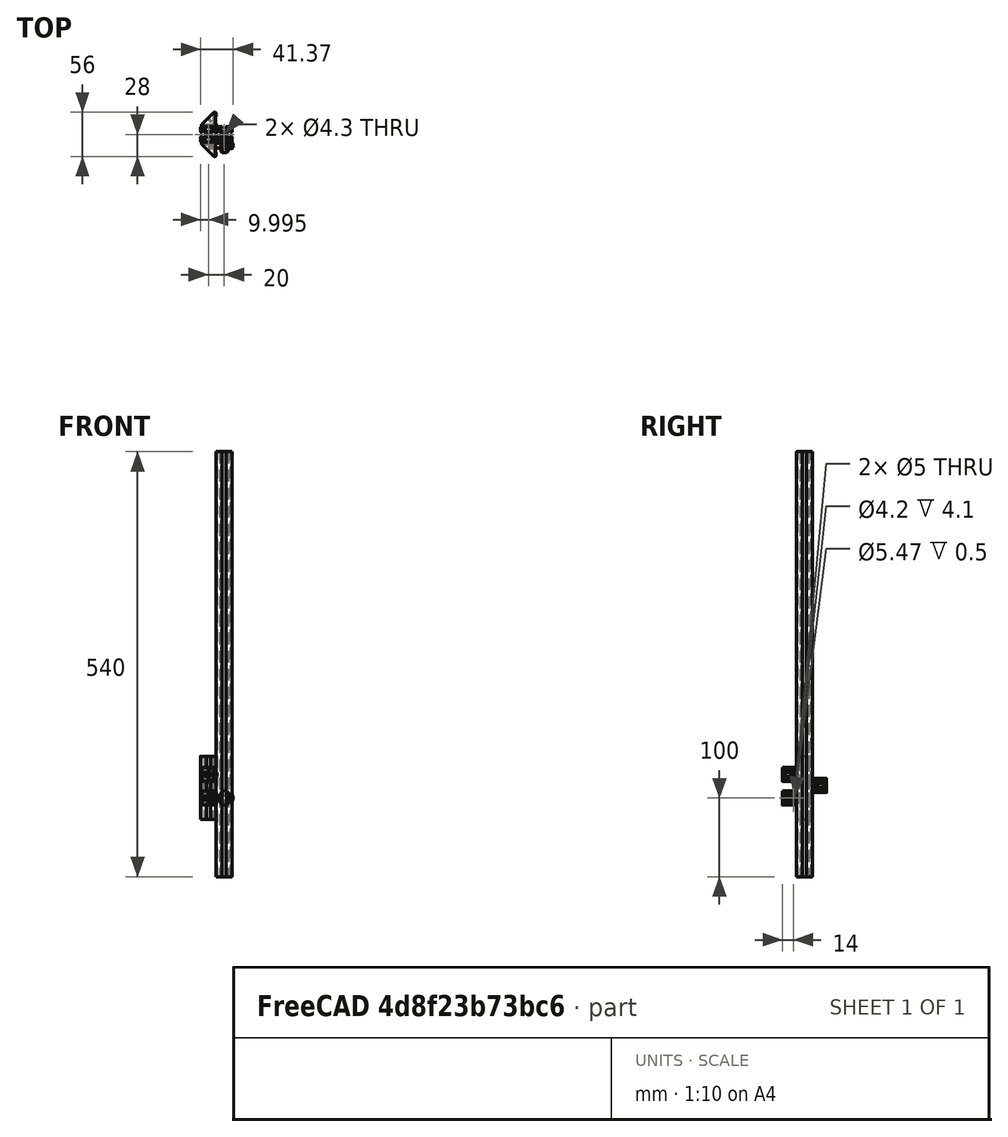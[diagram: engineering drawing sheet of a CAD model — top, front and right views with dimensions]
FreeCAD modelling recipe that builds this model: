
FCSTD DOCUMENT  (FreeCAD 0.19R)
Label: Cart
License: All rights reserved
LicenseURL: http://en.wikipedia.org/wiki/All_rights_reserved
objects: Part::Feature×11, Part::FeaturePython×6, App::Part×4, Part::Cylinder×3
note: 20 computed .brp shape members not serialized (recipe doc carries the construction recipe); baked Part::Feature solids carry a one-line shape summary decoded from their .brp

FEATURE [Part::FeaturePython] Screw001  label="M5x25-Screw"  # Fasteners workbench fastener (typed FeaturePython)
  Placement = pos=(-13,0,0) rot=(0,-1,0;1.5708rad)
  diameter = 3
  invert = false
  length = 5
  lengthCustom = 25
  matchOuter = false
  offset = 1
  thread = false
  type = 12
FEATURE [Part::Cylinder] Cylinder004  label="Spacer"
  Angle = 360
  AttacherType = Attacher::AttachEngine3D
  Height = 6
  Placement = pos=(-10,0,0) rot=(0,1,0;1.5708rad)
  Radius = 3.5
FEATURE [Part::Feature] Cut002  label="Tire"
  Placement = pos=(1,0,0) rot=(0,0,1;0rad)
  shape: bbox 8.8 x 18.03 x 18.03 mm, 6 faces (baked)
FEATURE [Part::Feature] Cut001001  label="Bearing"
  Placement = pos=(1,0,0) rot=(0,0,1;0rad)
  shape: bbox 10 x 10 x 10 mm, 4 faces (baked)
FEATURE [Part::FeaturePython] Nut  label="M5-Nut"  # Fasteners workbench fastener (typed FeaturePython)
  Placement = pos=(11,0,0) rot=(0,-1,0;1.5708rad)
  diameter = 3
  invert = false
  matchOuter = false
  offset = 0
  thread = false
  type = 5
FEATURE [App::Part] Part  label="Rollensatz_Aliexpress4000394459605"
  Group = -> [Screw001,Cut002,Cut001001,Cylinder004,Nut]
  Origin = -> Origin
  Placement = pos=(0,-4,0) rot=(0,0,1;0rad)
FEATURE [Part::FeaturePython] Nut001  label="M5-Nut001"  # Fasteners workbench fastener (typed FeaturePython)
  Placement = pos=(11,0,0) rot=(0,-1,0;1.5708rad)
  diameter = 3
  invert = false
  matchOuter = false
  offset = 0
  thread = false
  type = 5
FEATURE [Part::FeaturePython] Screw002  label="M5x25-Screw003"  # Fasteners workbench fastener (typed FeaturePython)
  Placement = pos=(-13,0,0) rot=(0,-1,0;1.5708rad)
  diameter = 3
  invert = false
  length = 5
  lengthCustom = 25
  matchOuter = false
  offset = 1
  thread = false
  type = 12
FEATURE [Part::Feature] Cut001002  label="Bearing001"
  Placement = pos=(1,0,0) rot=(0,0,1;0rad)
  shape: bbox 10 x 10 x 10 mm, 4 faces (baked)
FEATURE [Part::Feature] Cut001003  label="Tire001"
  Placement = pos=(1,0,0) rot=(0,0,1;0rad)
  shape: bbox 8.8 x 18.03 x 18.03 mm, 6 faces (baked)
FEATURE [Part::Cylinder] Cylinder005  label="Spacer001"
  Angle = 360
  AttacherType = Attacher::AttachEngine3D
  Height = 6
  Placement = pos=(-10,0,0) rot=(0,1,0;1.5708rad)
  Radius = 3.5
FEATURE [App::Part] Part001  label="Rollensatz_Aliexpress4000394459605_2"
  Group = -> [Screw002,Cut001003,Cut001002,Cylinder005,Nut001]
  Origin = -> Origin001
  Placement = pos=(0,-4,30) rot=(0,0,1;0rad)
FEATURE [Part::FeaturePython] Nut002  label="M5-Nut002"  # Fasteners workbench fastener (typed FeaturePython)
  Placement = pos=(11,0,0) rot=(0,-1,0;1.5708rad)
  diameter = 3
  invert = false
  matchOuter = false
  offset = 0
  thread = false
  type = 5
FEATURE [Part::FeaturePython] Screw003  label="M5x25-Screw004"  # Fasteners workbench fastener (typed FeaturePython)
  Placement = pos=(-13,0,0) rot=(0,-1,0;1.5708rad)
  diameter = 3
  invert = false
  length = 5
  lengthCustom = 25
  matchOuter = false
  offset = 1
  thread = false
  type = 12
FEATURE [Part::Feature] Cut001004  label="Bearing002"
  Placement = pos=(1,0,0) rot=(0,0,1;0rad)
  shape: bbox 10 x 10 x 10 mm, 4 faces (baked)
FEATURE [Part::Feature] Cut001005  label="Tire002"
  Placement = pos=(1,0,0) rot=(0,0,1;0rad)
  shape: bbox 8.8 x 18.03 x 18.03 mm, 6 faces (baked)
FEATURE [Part::Cylinder] Cylinder006  label="Spacer002"
  Angle = 360
  AttacherType = Attacher::AttachEngine3D
  Height = 6
  Placement = pos=(-10,0,0) rot=(0,1,0;1.5708rad)
  Radius = 3.5
FEATURE [App::Part] Part002  label="Rollensatz_Aliexpress4000394459605_3"
  Group = -> [Screw003,Cut001005,Cut001004,Cylinder006,Nut002]
  Origin = -> Origin002
  Placement = pos=(0,33,15) rot=(0,0,1;0rad)
FEATURE [Part::Feature] Extrude001001  label="540Profile_20x20slot5"
  Placement = pos=(4,24,-600) rot=(0,0,1;0rad)
  shape: bbox 20 x 20 x 540 mm, 75 faces (baked)
FEATURE [Part::Feature] Extrude001002  label="15cmProfile_15x15"
  Placement = pos=(-16,24,-527) rot=(0,0,1;0rad)
  shape: bbox 20 x 20 x 80 mm, 75 faces (baked)
FEATURE [Part::Feature] Solid001  label="M5WinkelProfile20x20"
  Placement = pos=(-10,4,0) rot=(0,0,1;1.5708rad)
  shape: bbox 19.8 x 19.8 x 18 mm, 176 faces (baked)
FEATURE [Part::Feature] Solid002  label="M5WinkelProfile20x20_2"
  Placement = pos=(-10,4,30) rot=(0,0,1;1.5708rad)
  shape: bbox 19.8 x 19.8 x 18 mm, 176 faces (baked)
FEATURE [Part::Feature] Solid003  label="M5WinkelProfile20x20_3"
  Placement = pos=(-10,24,16) rot=(-0.707107,0.707107,0;3.14159rad)
  shape: bbox 19.8 x 19.8 x 18 mm, 176 faces (baked)
FEATURE [App::Part] Part003  label="Cart"
  Group = -> [Part,Part001,Part002,Extrude001002,Solid001,Solid002,Solid003]
  Origin = -> Origin003
